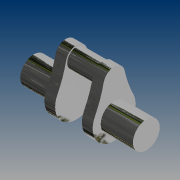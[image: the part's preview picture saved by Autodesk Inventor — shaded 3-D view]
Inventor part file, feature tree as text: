
AUTODESK INVENTOR PART (.ipt)
format: ipt  version: 2014 (Build 180170000, 170)  size: 125,440 bytes
history: native  units: mm
features: extrude x3, sketch x3, mirror x2, plane x1
ambient origin geometry x8: Origin, YZ Plane, XZ Plane, XY Plane, X Axis, Y Axis, Z Axis, Center Point
bodies: Body1 (feature_tree)
feature tree (9):
  extrude  "Extrusion4"  Depth=40.0mm
  extrude  "Extrusion5"  Depth=200.0mm
  extrude  "Extrusion6"  Depth=20.0mm TaperAngle=0.0deg
  plane  "Work Plane2"
  mirror  "Mirror3"
  mirror  "Mirror4"
  sketch  "Sketch4"  dims[d13=80.0mm d14=40.0mm]
  sketch  "Sketch5"  dims[d15=60.0mm d16=200.0mm]
  sketch  "Sketch6"  dims[d17=200.0mm d18=20.0mm d19=0.0mm d20=50.0mm d21=60.0mm d22=0.0mm d23=35.0mm d24=50.0mm d25=0.0mm]
